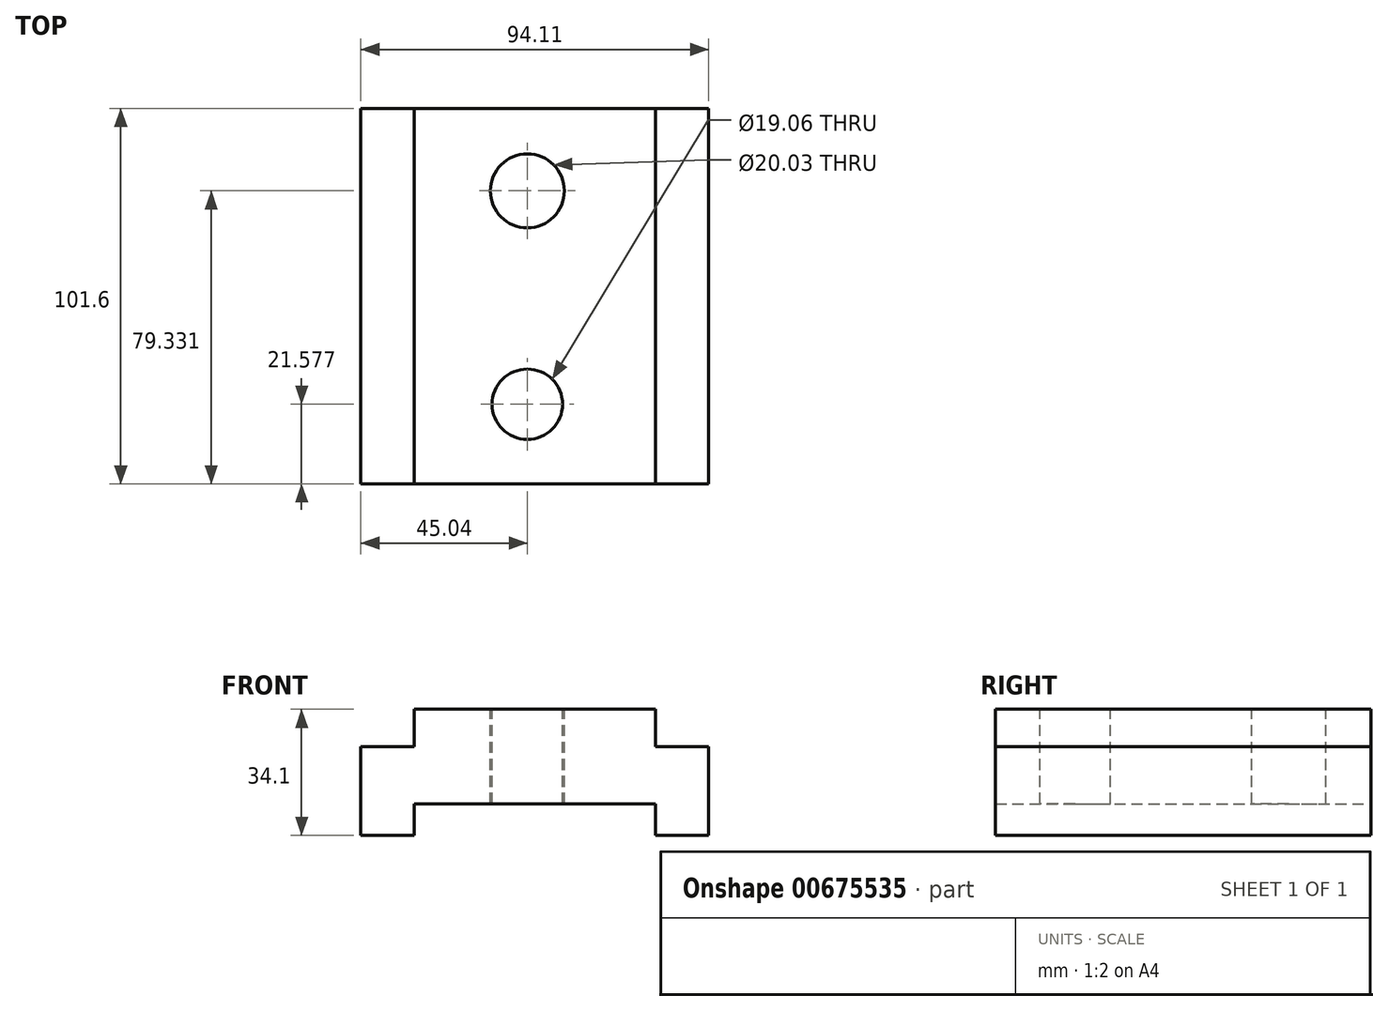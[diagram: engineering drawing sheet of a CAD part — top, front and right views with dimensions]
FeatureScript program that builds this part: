
annotation { "Feature Type Name" : "Feature", "Feature Type Description" : "" }
export const myFeature = defineFeature(function(context is Context, id is Id, definition is map)
    precondition{}
    {
        {
            var Q0;
            Q0=qCreatedBy(makeId("Front.planeOp"),FACE);
            var sketch = newSketch(context, id + "F0", { "sketchPlane" : qUnion([Q0])});
            skLineSegment(sketch, "E0", {"start": v(-30.65, 34.1) * mm, "end": v(34.68, 34.1) * mm});
            skLineSegment(sketch, "E1", {"start": v(34.68, 34.1) * mm, "end": v(34.68, 24.03) * mm});
            skLineSegment(sketch, "E2", {"start": v(34.68, 24.03) * mm, "end": v(49.07, 24.03) * mm});
            skLineSegment(sketch, "E3", {"start": v(49.07, 24.03) * mm, "end": v(49.07, 0) * mm});
            skLineSegment(sketch, "E4", {"start": v(49.07, 0) * mm, "end": v(34.68, 0) * mm});
            skLineSegment(sketch, "E5", {"start": v(34.68, 0) * mm, "end": v(34.68, 8.5) * mm});
            skLineSegment(sketch, "E6", {"start": v(34.68, 8.5) * mm, "end": v(-30.65, 8.5) * mm});
            skLineSegment(sketch, "E7", {"start": v(-30.65, 8.5) * mm, "end": v(-30.65, 0) * mm});
            skLineSegment(sketch, "E8", {"start": v(-30.65, 0) * mm, "end": v(-45.04, 0) * mm});
            skLineSegment(sketch, "E9", {"start": v(-45.04, 0) * mm, "end": v(-45.04, 24.03) * mm});
            skLineSegment(sketch, "E10", {"start": v(-45.04, 24.03) * mm, "end": v(-30.65, 24.03) * mm});
            skLineSegment(sketch, "E11", {"start": v(-30.65, 24.03) * mm, "end": v(-30.65, 34.1) * mm});
            skSolve(sketch);
        }
        {
            var Q0;
            Q0 = qSketchRegion(id + "F0", true);
            extrude(context, id + "F1", {"entities" : qUnion([Q0]), "depth" : 101.6 * mm, "offsetDistance" : 25.4 * mm});
        }
        {
            var Q0;
            Q0=makeQuery(id+"F1.opExtrude","SWEPT_FACE",FACE,{"disambiguationData":[OSD([sQuery(id+"F0.wireOp",EDGE,"E0")])]});
            var sketch = newSketch(context, id + "F2", { "sketchPlane" : qUnion([Q0])});
            skCircle(sketch, "E12", {"center": v(0, -22.27) * mm, "radius": 10.01 * mm});
            skCircle(sketch, "E13", {"center": v(0, -80.02) * mm, "radius": 9.53 * mm});
            skSolve(sketch);
        }
        {
            var Q0;
            Q0 = qSketchRegion(id + "F2", true);
            extrude(context, id + "F3", {"entities" : qUnion([Q0]), "operationType" : NewBodyOperationType.REMOVE, "oppositeDirection" : true, "depth" : 76.2 * mm, "offsetDistance" : 25.4 * mm});
        }
    });
